# Revit family: Multi Container Bracket Assy-JCI_Sapphire_Plus-(70 bar) Novec1230
name_source: partatom
category: Specialty Equipment
revit_build: Autodesk Revit 2017 (Build: 20171027_0315(x64)
units: mm (PartAtom-declared; Revit-internal decimal feet)

## family parameters
Always vertical = No
Cut with Voids When Loaded = No
OmniClass Number = 23.29.33.13.11
Part Type = Normal
Room Calculation Point = No
Round Connector Dimension = Use Diameter
Shared = No
Work Plane-Based = Yes

## types (6) — shared parameters
Date Modified = YYYY/MM/DD
Description = Container Bracket Assembly-Sapphire Plus
Diameter = 47.6 mm  [stored 0.156168 ft]
Discharge Flow = 0 GPM
Equipment Abbreviation = MCB
Equipment Number = XXX
Family Version = 1.0
Fire Suppression Agent = 3M™ Novec™ 1230 Fire Protection Fluid
Height = 41 mm  [stored 0.134514 ft]
Length = 47.6 mm  [stored 0.156168 ft]
Manufacturer = Johnson Controls, Inc.
Model Disclaimer = For More Information Contact JOHNSON CONTROLS
Part Description = Container Bracket Assembly-Sapphire Plus
Pipe Diameter = 12.7 mm  [stored 0.0416667 ft]
URL = http://www.sapphireplus.com
Width = 47.6 mm  [stored 0.156168 ft]
zero-valued in all types: Default Elevation

## per-type parameters (varying)
| type | Container Bracket Assy Type | Material | Model | Part Number | Product Documentation Link | Product Page URL | Type Comments |
| 120-150 L x 4 | Container Bracket Assy-JCI_Sapphire_Plus-(70 bar) Novec1230 : 120-150 L x 4 | JCI - Metal - Brass - Satin | 311700007 | 311700007 |  |  | 311700007 |
| 120-150 L x 6 | Container Bracket Assy-JCI_Sapphire_Plus-(70 bar) Novec1230 : 120-150 L x 6 | JCI - Metal - Steel | 311700008 | 311700008 |  |  | 311700008 |
| 120-150 L x 8 | Container Bracket Assy-JCI_Sapphire_Plus-(70 bar) Novec1230 : 120-150 L x 8 | JCI - Metal - Brass - Satin | 311700009 | 311700009 |  |  | 311700009 |
| PESO 120-180 L x 4 | Container Bracket Assy-JCI_Sapphire_Plus-(70 bar) Novec1230 : PESO 120-180 L x 4 | JCI - Metal - Brass - Satin | 311700010 | 311700010 | http://www.sapphireplus.com | http://www.sapphireplus.com | 311700010 |
| PESO 120-180 L x 6 | Container Bracket Assy-JCI_Sapphire_Plus-(70 bar) Novec1230 : PESO 120-180 L x 6 | JCI - Metal - Brass - Satin | 311700011 | 311700011 |  |  | 311700011 |
| PESO 120-180 L x 8 | Container Bracket Assy-JCI_Sapphire_Plus-(70 bar) Novec1230 : PESO 120-180 L x 8 | JCI - Metal - Steel | 311700012 | 311700012 |  |  | 311700012 |

note: [stored X ft] marks values corroborated as IEEE doubles in the binary element streams (Revit-internal decimal feet)

## geometry (parser evidence)
native form markers: Sweep x8
no freeform markers — native parametric forms only
